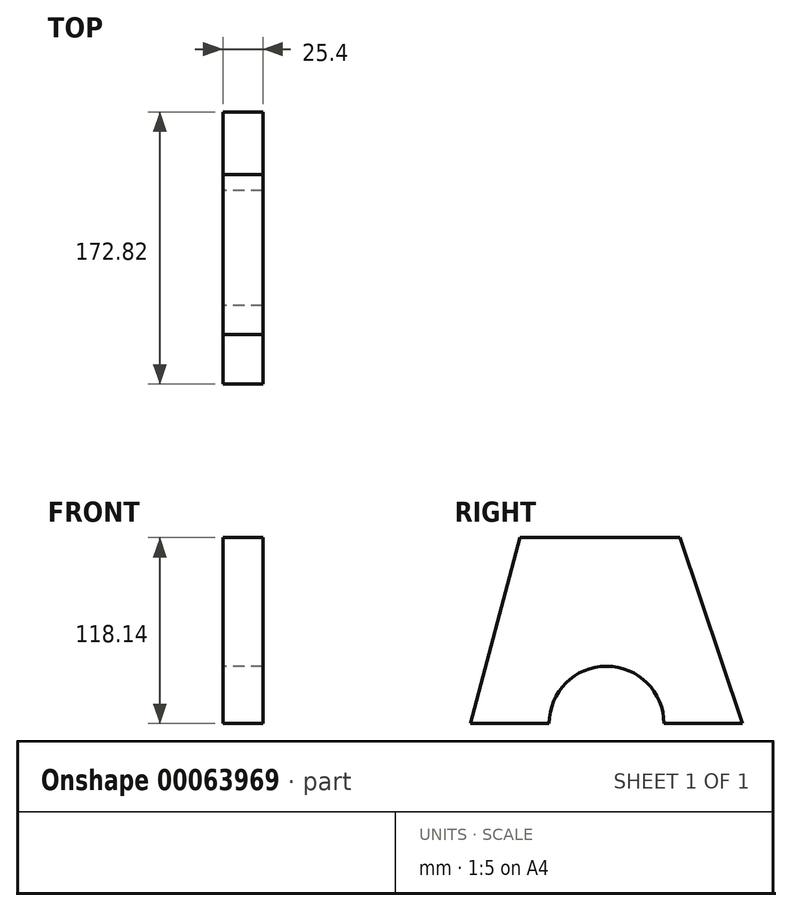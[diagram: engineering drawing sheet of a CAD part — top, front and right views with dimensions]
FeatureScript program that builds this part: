
annotation { "Feature Type Name" : "Feature", "Feature Type Description" : "" }
export const myFeature = defineFeature(function(context is Context, id is Id, definition is map)
    precondition{}
    {
        {
            var Q0;
            Q0=qCreatedBy(makeId("Right.planeOp"),FACE);
            var sketch = newSketch(context, id + "F0", { "sketchPlane" : qUnion([Q0])});
            skLineSegment(sketch, "E0", {"start": v(-54.76, 48.34) * mm, "end": v(46.84, 48.34) * mm});
            skLineSegment(sketch, "E1", {"start": v(46.84, 48.34) * mm, "end": v(86.67, -69.8) * mm});
            skLineSegment(sketch, "E2", {"start": v(86.67, -69.8) * mm, "end": v(36.7, -69.8) * mm});
            skLineSegment(sketch, "E3", {"start": v(-86.15, -69.8) * mm, "end": v(-54.76, 48.34) * mm});
            skArc(sketch, "E4", {"start": v(36.7, -69.8) * mm, "mid": v(0.26, -33.35) * mm, "end": v(-36.2, -69.8) * mm});
            skLineSegment(sketch, "E5.trimOffspring", {"start": v(-36.2, -69.8) * mm, "end": v(-86.15, -69.8) * mm});
            skLineSegment(sketch, "E6", {"start": v(-86.15, -69.8) * mm, "end": v(-86.15, 48.34) * mm, "construction": true});
            skLineSegment(sketch, "E7", {"start": v(-86.15, 48.34) * mm, "end": v(-54.76, 48.34) * mm, "construction": true});
            skSolve(sketch);
        }
        {
            var Q0;
            Q0 = qSketchRegion(id + "F0", true);
            extrude(context, id + "F1", {"entities" : qUnion([Q0]), "depth" : 25.4 * mm});
        }
    });
